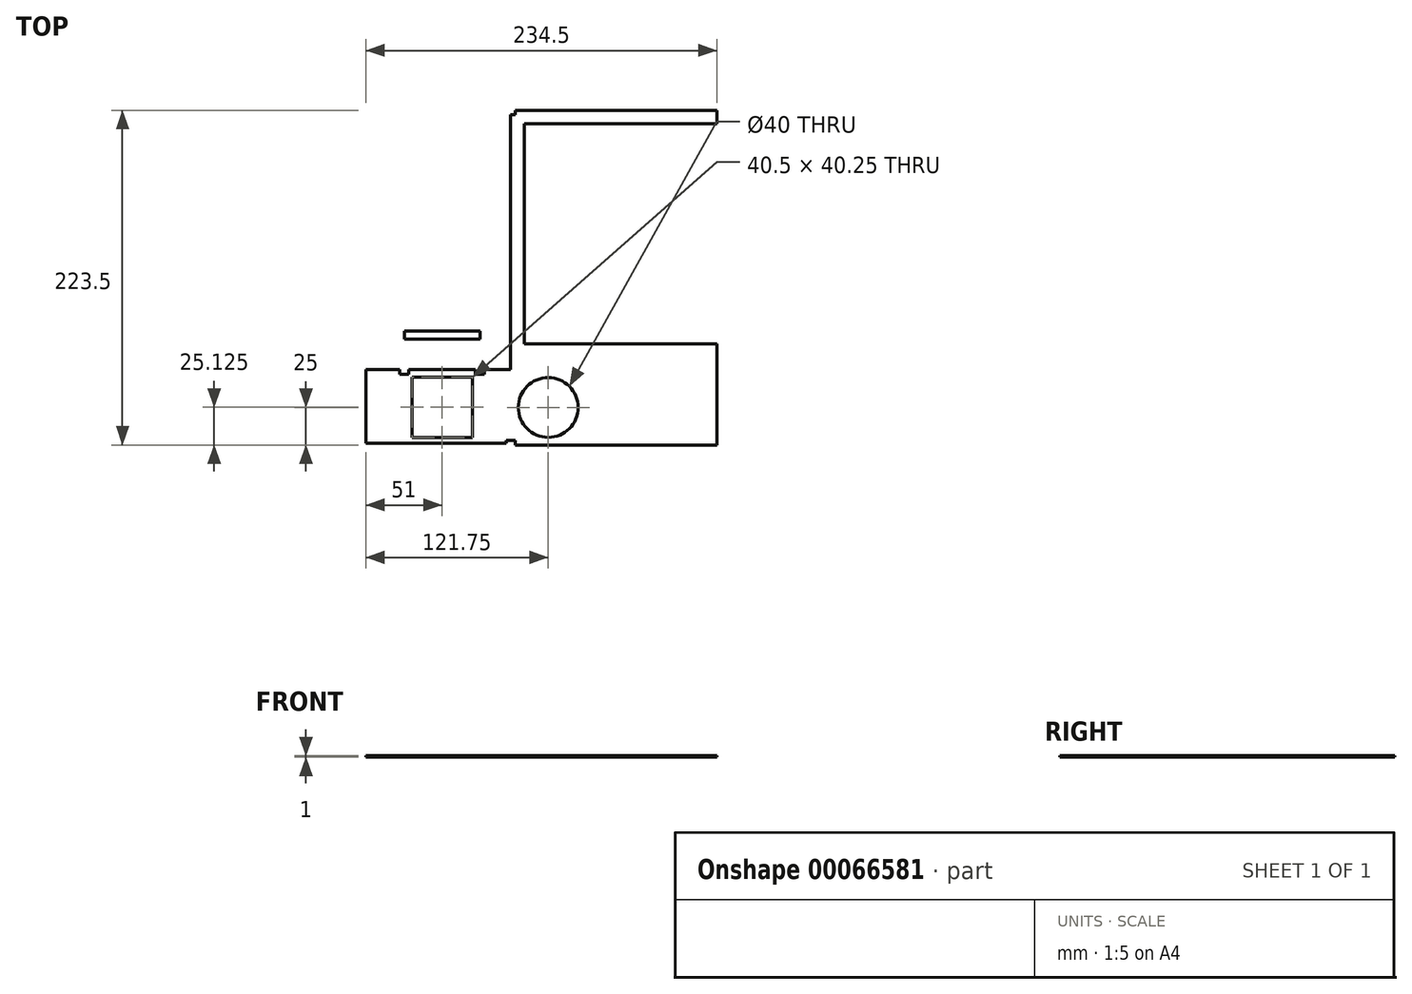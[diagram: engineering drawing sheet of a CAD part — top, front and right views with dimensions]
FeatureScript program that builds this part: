
annotation { "Feature Type Name" : "Feature", "Feature Type Description" : "" }
export const myFeature = defineFeature(function(context is Context, id is Id, definition is map)
    precondition{}
    {
        {
            var Q0;
            Q0=qCreatedBy(makeId("Top.planeOp"),FACE);
            var sketch = newSketch(context, id + "F0", { "sketchPlane" : qUnion([Q0])});
            skLineSegment(sketch, "E0.rect.bottom", {"start": v(0, 111) * mm, "end": v(-137.75, 111) * mm});
            skLineSegment(sketch, "E0.rect.top", {"start": v(0, -112.5) * mm, "end": v(-137.75, -112.5) * mm});
            skLineSegment(sketch, "E0.rect.right", {"start": v(-137.75, 111) * mm, "end": v(-137.75, -112.5) * mm});
            skPoint(sketch, "E0.rect.middle", {"position": v(0, 0) * mm});
            skLineSegment(sketch, "E1.bottom", {"start": v(-128.75, 102) * mm, "end": v(0, 102) * mm});
            skLineSegment(sketch, "E1.top", {"start": v(-128.75, -45) * mm, "end": v(0, -45) * mm});
            skLineSegment(sketch, "E1.left", {"start": v(-128.75, 102) * mm, "end": v(-128.75, -45) * mm});
            skCircle(sketch, "E2", {"center": v(-112.75, -87.5) * mm, "radius": 20 * mm});
            skLineSegment(sketch, "E3", {"start": v(0, 111) * mm, "end": v(0, -112.5) * mm});
            skLineSegment(sketch, "E4.bottom", {"start": v(-137.75, -112.5) * mm, "end": v(-158.25, -112.5) * mm});
            skLineSegment(sketch, "E4.top", {"start": v(-137.75, -62.25) * mm, "end": v(-158.25, -62.25) * mm});
            skLineSegment(sketch, "E4.left", {"start": v(-137.75, -112.5) * mm, "end": v(-137.75, -62.25) * mm});
            skLineSegment(sketch, "E4.right", {"start": v(-158.25, -112.5) * mm, "end": v(-158.25, -62.25) * mm});
            skLineSegment(sketch, "E5.bottom", {"start": v(-158.25, -62.25) * mm, "end": v(-208.75, -62.25) * mm});
            skLineSegment(sketch, "E5.top", {"start": v(-158.25, -112.5) * mm, "end": v(-208.75, -112.5) * mm});
            skLineSegment(sketch, "E5.left", {"start": v(-158.25, -62.25) * mm, "end": v(-158.25, -112.5) * mm});
            skLineSegment(sketch, "E5.right", {"start": v(-208.75, -62.25) * mm, "end": v(-208.75, -112.5) * mm});
            skLineSegment(sketch, "E6.bottom", {"start": v(-208.75, -62.25) * mm, "end": v(-229.25, -62.25) * mm});
            skLineSegment(sketch, "E6.top", {"start": v(-208.75, -112.5) * mm, "end": v(-229.25, -112.5) * mm});
            skLineSegment(sketch, "E6.right", {"start": v(-229.25, -62.25) * mm, "end": v(-229.25, -112.5) * mm});
            skLineSegment(sketch, "E7.bottom", {"start": v(-208.75, -62.25) * mm, "end": v(-158.25, -62.25) * mm});
            skLineSegment(sketch, "E7.top", {"start": v(-208.75, -41.75) * mm, "end": v(-158.25, -41.75) * mm});
            skLineSegment(sketch, "E7.left", {"start": v(-208.75, -62.25) * mm, "end": v(-208.75, -41.75) * mm});
            skLineSegment(sketch, "E7.right", {"start": v(-158.25, -62.25) * mm, "end": v(-158.25, -41.75) * mm});
            skLineSegment(sketch, "E8.bottom", {"start": v(-229.25, -62.25) * mm, "end": v(-234.5, -62.25) * mm});
            skLineSegment(sketch, "E8.top", {"start": v(-229.25, -112.5) * mm, "end": v(-234.5, -112.5) * mm});
            skLineSegment(sketch, "E8.right", {"start": v(-234.5, -62.25) * mm, "end": v(-234.5, -112.5) * mm});
            skLineSegment(sketch, "E9.bottom", {"start": v(-203.75, -67.25) * mm, "end": v(-163.25, -67.25) * mm});
            skLineSegment(sketch, "E9.top", {"start": v(-203.75, -107.5) * mm, "end": v(-163.25, -107.5) * mm});
            skLineSegment(sketch, "E9.left", {"start": v(-203.75, -67.25) * mm, "end": v(-203.75, -107.5) * mm});
            skLineSegment(sketch, "E9.right", {"start": v(-163.25, -67.25) * mm, "end": v(-163.25, -107.5) * mm});
            skLineSegment(sketch, "E10.bottom", {"start": v(-137.75, -62.25) * mm, "end": v(-142, -62.25) * mm});
            skLineSegment(sketch, "E10.top", {"start": v(-137.75, 111) * mm, "end": v(-142, 111) * mm});
            skLineSegment(sketch, "E10.left", {"start": v(-137.75, -62.25) * mm, "end": v(-137.75, 111) * mm});
            skLineSegment(sketch, "E10.right", {"start": v(-142, -62.25) * mm, "end": v(-142, 111) * mm});
            skLineSegment(sketch, "E11.bottom", {"start": v(-137.75, -112.5) * mm, "end": v(0, -112.5) * mm});
            skLineSegment(sketch, "E11.top", {"start": v(-137.75, -132.75) * mm, "end": v(0, -132.75) * mm});
            skLineSegment(sketch, "E11.left", {"start": v(-137.75, -112.5) * mm, "end": v(-137.75, -132.75) * mm});
            skLineSegment(sketch, "E11.right", {"start": v(0, -112.5) * mm, "end": v(0, -132.75) * mm});
            skLineSegment(sketch, "E12", {"start": v(0, -112.5) * mm, "end": v(0, 111) * mm});
            skLineSegment(sketch, "E13.top", {"start": v(-208.75, -36.5) * mm, "end": v(-158.25, -36.5) * mm});
            skLineSegment(sketch, "E13.left", {"start": v(-208.75, -41.75) * mm, "end": v(-208.75, -36.5) * mm});
            skLineSegment(sketch, "E13.right", {"start": v(-158.25, -41.75) * mm, "end": v(-158.25, -36.5) * mm});
            skLineSegment(sketch, "E14.bottom", {"start": v(-137.75, 111) * mm, "end": v(0, 111) * mm});
            skLineSegment(sketch, "E14.top", {"start": v(-137.75, 115.25) * mm, "end": v(0, 115.25) * mm});
            skLineSegment(sketch, "E14.left", {"start": v(-137.75, 111) * mm, "end": v(-137.75, 115.25) * mm});
            skLineSegment(sketch, "E14.right", {"start": v(0, 111) * mm, "end": v(0, 115.25) * mm});
            skSolve(sketch);
        }
        {
            var Q0;
            Q0=makeQuery(id+"F0.imprint","IMPRINT",FACE,{"disambiguationData":[TD([[makeQuery(id+"F0.imprint","IMPRINT",EDGE,{"derivedFrom":sQuery(id+"F0.wireOp",EDGE,"E8.bottom")}),1.0]])]});
            var Q1;
            Q1=makeQuery(id+"F0.imprint","IMPRINT",FACE,{"disambiguationData":[TD([[makeQuery(id+"F0.imprint","IMPRINT",EDGE,{"derivedFrom":sQuery(id+"F0.wireOp",EDGE,"E11.bottom")}),-1.0]])]});
            var Q2;
            Q2=makeQuery(id+"F0.imprint","IMPRINT",FACE,{"disambiguationData":[TD([[makeQuery(id+"F0.imprint","IMPRINT",EDGE,{"derivedFrom":sQuery(id+"F0.wireOp",EDGE,"E7.top")}),1.0]])]});
            var Q3;
            Q3=makeQuery(id+"F0.imprint","IMPRINT",FACE,{"disambiguationData":[TD([[makeQuery(id+"F0.imprint","IMPRINT",EDGE,{"derivedFrom":sQuery(id+"F0.wireOp",EDGE,"E14.bottom")}),1.0]])]});
            var Q4;
            Q4=makeQuery(id+"F0.imprint","IMPRINT",FACE,{"disambiguationData":[TD([[makeQuery(id+"F0.imprint","IMPRINT",EDGE,{"derivedFrom":sQuery(id+"F0.wireOp",EDGE,"E6.bottom")}),1.0]])]});
            var Q5;
            Q5=makeQuery(id+"F0.imprint","IMPRINT",FACE,{"disambiguationData":[TD([[makeQuery(id+"F0.imprint","IMPRINT",EDGE,{"derivedFrom":sQuery(id+"F0.wireOp",EDGE,"E7.bottom")}),1.0]])]});
            var Q6;
            Q6=makeQuery(id+"F0.imprint","IMPRINT",FACE,{"disambiguationData":[TD([[makeQuery(id+"F0.imprint","IMPRINT",EDGE,{"derivedFrom":sQuery(id+"F0.wireOp",EDGE,"E10.bottom")}),-1.0]])]});
            var Q7;
            Q7=makeQuery(id+"F0.imprint","IMPRINT",FACE,{"disambiguationData":[TD([[makeQuery(id+"F0.imprint","IMPRINT",EDGE,{"derivedFrom":sQuery(id+"F0.wireOp",EDGE,"E4.bottom")}),-1.0]])]});
            var Q8;
            Q8=makeQuery(id+"F0.imprint","IMPRINT",FACE,{"disambiguationData":[TD([[makeQuery(id+"F0.imprint","IMPRINT",EDGE,{"derivedFrom":sQuery(id+"F0.wireOp",EDGE,"E5.top")}),-1.0]])]});
            var Q9;
            {var subQ1=sQuery(id+"F0.wireOp",EDGE,"E1.bottom");Q9=makeQuery(id+"F0.imprint","IMPRINT",FACE,{"disambiguationData":[TD([[makeQuery(id+"F0.imprint","IMPRINT",EDGE,{"derivedFrom":subQ1}),1.0]])]});}
            extrude(context, id + "F1", {"entities" : qUnion([Q0, Q1, Q2, Q3, Q4, Q5, Q6, Q7, Q8, Q9]), "depth" : 1 * mm});
        }
        {
            var Q0;
            {var subQ0=sQuery(id+"F0.wireOp",EDGE,"E14.right");var subQ1=sQuery(id+"F0.wireOp",EDGE,"E14.left");var subQ2=sQuery(id+"F0.wireOp",EDGE,"E14.top");var subQ3=sQuery(id+"F0.wireOp",EDGE,"E13.right");var subQ4=sQuery(id+"F0.wireOp",EDGE,"E13.left");var subQ5=sQuery(id+"F0.wireOp",EDGE,"E13.top");var subQ6=sQuery(id+"F0.wireOp",EDGE,"E12");var subQ7=sQuery(id+"F0.wireOp",EDGE,"E11.right");var subQ8=sQuery(id+"F0.wireOp",EDGE,"E11.left");var subQ9=sQuery(id+"F0.wireOp",EDGE,"E11.top");var subQ10=sQuery(id+"F0.wireOp",EDGE,"E10.right");var subQ11=sQuery(id+"F0.wireOp",EDGE,"E10.top");var subQ12=sQuery(id+"F0.wireOp",EDGE,"E9.right");var subQ13=sQuery(id+"F0.wireOp",EDGE,"E9.left");var subQ14=sQuery(id+"F0.wireOp",EDGE,"E9.top");var subQ15=sQuery(id+"F0.wireOp",EDGE,"E9.bottom");var subQ16=sQuery(id+"F0.wireOp",EDGE,"E8.right");var subQ17=sQuery(id+"F0.wireOp",EDGE,"E8.top");var subQ18=sQuery(id+"F0.wireOp",EDGE,"E8.bottom");var subQ19=sQuery(id+"F0.wireOp",EDGE,"E7.right");var subQ20=sQuery(id+"F0.wireOp",EDGE,"E7.left");var subQ21=sQuery(id+"F0.wireOp",EDGE,"E6.top");var subQ22=sQuery(id+"F0.wireOp",EDGE,"E6.bottom");var subQ23=sQuery(id+"F0.wireOp",EDGE,"E5.top");var subQ24=sQuery(id+"F0.wireOp",EDGE,"E4.top");var subQ25=sQuery(id+"F0.wireOp",EDGE,"E4.bottom");var subQ26=sQuery(id+"F0.wireOp",EDGE,"E2");Q0=makeQuery(id+"FCeXNnp2rNS88lh_0.boolean.opBoolean","MERGE",FACE,{"derivedFrom":[makeQuery(id+"F1.opExtrude","CAP_FACE",FACE,{"disambiguationData":[OSD([sQuery(id+"F0.wireOp",EDGE,"E1.bottom"),sQuery(id+"F0.wireOp",EDGE,"E1.top"),sQuery(id+"F0.wireOp",EDGE,"E1.left"),subQ26,subQ25,subQ24,subQ23,subQ22,subQ21,subQ20,subQ19,subQ18,subQ17,subQ16,subQ15,subQ14,subQ13,subQ12,subQ11,subQ10,subQ9,subQ8,subQ7,subQ6,subQ5,subQ4,subQ3,subQ2,subQ1,subQ0])],"isStart":false}),makeQuery(id+"FCeXNnp2rNS88lh_0.opExtrude","CAP_FACE",FACE,{"disambiguationData":[OSD([subQ26,subQ25,subQ24,subQ23,subQ22,subQ21,subQ20,subQ19,subQ18,subQ17,subQ16,subQ15,subQ14,subQ13,subQ12,subQ11,subQ10,subQ9,subQ8,subQ7,subQ6,subQ5,subQ4,subQ3,subQ2,subQ1,subQ0])],"isStart":false})]});}
            var sketch = newSketch(context, id + "F2", { "sketchPlane" : qUnion([Q0])});
            skLineSegment(sketch, "E15.rect.bottom", {"start": v(-134.75, -109.5) * mm, "end": v(-140.75, -109.5) * mm});
            skLineSegment(sketch, "E15.rect.top", {"start": v(-134.75, -115.5) * mm, "end": v(-140.75, -115.5) * mm});
            skLineSegment(sketch, "E15.rect.left", {"start": v(-134.75, -109.5) * mm, "end": v(-134.75, -115.5) * mm});
            skLineSegment(sketch, "E15.rect.right", {"start": v(-140.75, -109.5) * mm, "end": v(-140.75, -115.5) * mm});
            skPoint(sketch, "E15.rect.middle", {"position": v(-137.75, -112.5) * mm});
            skLineSegment(sketch, "E16.rect.bottom", {"start": v(-155.25, -59.25) * mm, "end": v(-161.25, -59.25) * mm});
            skLineSegment(sketch, "E16.rect.top", {"start": v(-155.25, -65.25) * mm, "end": v(-161.25, -65.25) * mm});
            skLineSegment(sketch, "E16.rect.left", {"start": v(-155.25, -59.25) * mm, "end": v(-155.25, -65.25) * mm});
            skLineSegment(sketch, "E16.rect.right", {"start": v(-161.25, -59.25) * mm, "end": v(-161.25, -65.25) * mm});
            skPoint(sketch, "E16.rect.middle", {"position": v(-158.25, -62.25) * mm});
            skLineSegment(sketch, "E17.rect.bottom", {"start": v(-205.75, -59.25) * mm, "end": v(-211.75, -59.25) * mm});
            skLineSegment(sketch, "E17.rect.top", {"start": v(-205.75, -65.25) * mm, "end": v(-211.75, -65.25) * mm});
            skLineSegment(sketch, "E17.rect.left", {"start": v(-205.75, -59.25) * mm, "end": v(-205.75, -65.25) * mm});
            skLineSegment(sketch, "E17.rect.right", {"start": v(-211.75, -59.25) * mm, "end": v(-211.75, -65.25) * mm});
            skPoint(sketch, "E17.rect.middle", {"position": v(-208.75, -62.25) * mm});
            skLineSegment(sketch, "E18.rect.bottom", {"start": v(-134.75, 114) * mm, "end": v(-140.75, 114) * mm});
            skLineSegment(sketch, "E18.rect.top", {"start": v(-134.75, 108) * mm, "end": v(-140.75, 108) * mm});
            skLineSegment(sketch, "E18.rect.left", {"start": v(-134.75, 114) * mm, "end": v(-134.75, 108) * mm});
            skLineSegment(sketch, "E18.rect.right", {"start": v(-140.75, 114) * mm, "end": v(-140.75, 108) * mm});
            skPoint(sketch, "E18.rect.middle", {"position": v(-137.75, 111) * mm});
            skLineSegment(sketch, "E19.bottom", {"start": v(-234.5, -112.5) * mm, "end": v(-137.75, -112.5) * mm});
            skLineSegment(sketch, "E19.top", {"start": v(-234.5, -111.5) * mm, "end": v(-137.75, -111.5) * mm});
            skLineSegment(sketch, "E19.left", {"start": v(-234.5, -112.5) * mm, "end": v(-234.5, -111.5) * mm});
            skLineSegment(sketch, "E19.right", {"start": v(-137.75, -112.5) * mm, "end": v(-137.75, -111.5) * mm});
            skSolve(sketch);
        }
        {
            var Q0;
            Q0=qSketchRegion(id+"F2",true);
            extrude(context, id + "F3", {"entities" : qUnion([Q0]), "operationType" : NewBodyOperationType.REMOVE, "oppositeDirection" : true, "depth" : 25 * mm});
        }
    });
